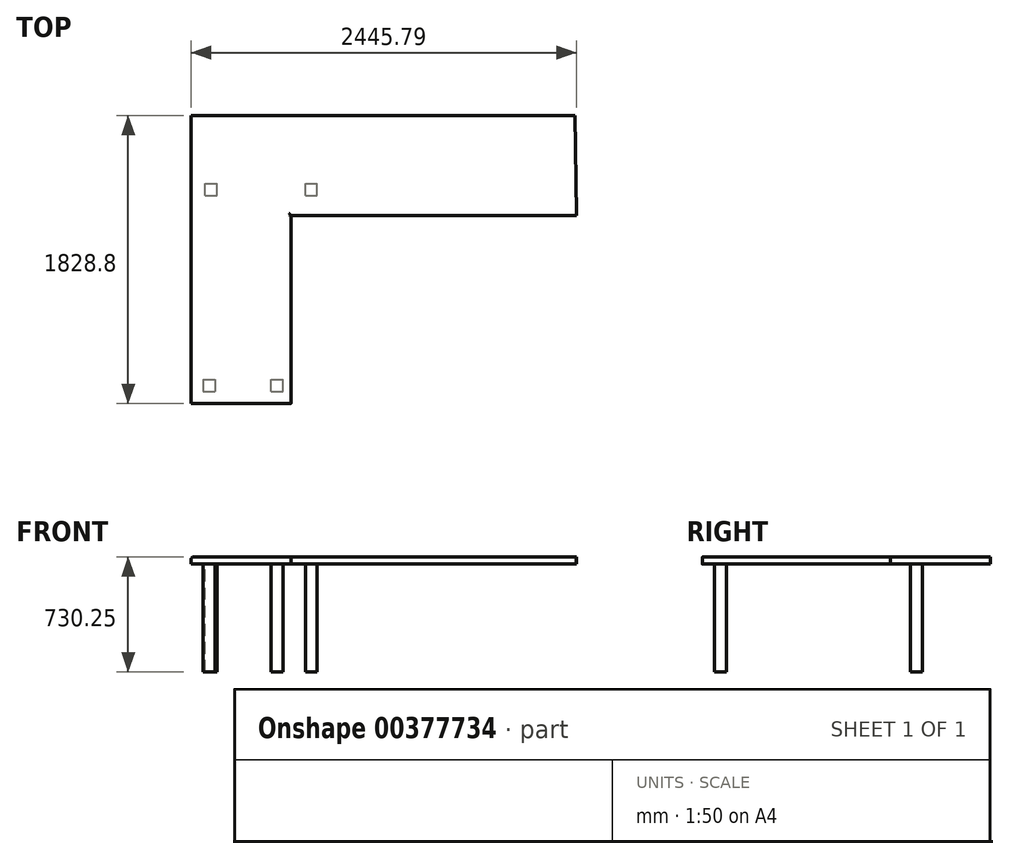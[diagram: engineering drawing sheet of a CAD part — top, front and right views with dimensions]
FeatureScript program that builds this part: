
annotation { "Feature Type Name" : "Feature", "Feature Type Description" : "" }
export const myFeature = defineFeature(function(context is Context, id is Id, definition is map)
    precondition{}
    {
        {
            var Q0;
            Q0=qCreatedBy(makeId("Top.planeOp"),FACE);
            var sketch = newSketch(context, id + "F0", { "sketchPlane" : qUnion([Q0])});
            skLineSegment(sketch, "E0", {"start": v(2399.33, 1785.57) * mm, "end": v(-39.07, 1785.57) * mm});
            skLineSegment(sketch, "E1", {"start": v(-39.07, 1785.57) * mm, "end": v(-39.07, -43.23) * mm});
            skLineSegment(sketch, "E2", {"start": v(-39.07, -43.23) * mm, "end": v(595.93, -43.23) * mm});
            skLineSegment(sketch, "E3", {"start": v(595.93, -43.23) * mm, "end": v(595.93, 1150.61) * mm});
            skLineSegment(sketch, "E4", {"start": v(595.93, 1150.61) * mm, "end": v(2406.72, 1150.61) * mm});
            skLineSegment(sketch, "E5", {"start": v(2406.72, 1150.61) * mm, "end": v(2399.33, 1785.57) * mm});
            skSolve(sketch);
        }
        {
            var Q0;
            Q0 = qSketchRegion(id + "F0", true);
            extrude(context, id + "F1", {"entities" : qUnion([Q0]), "depth" : 44.45 * mm});
        }
        {
            var Q0;
            Q0=makeQuery(id+"F1.opExtrude","CAP_EDGE",EDGE,{"disambiguationData":[OSD([sQuery(id+"F0.wireOp",EDGE,"E3")])],"isStart":false});
            var Q1;
            Q1=makeQuery(id+"F1.opExtrude","CAP_EDGE",EDGE,{"disambiguationData":[OSD([sQuery(id+"F0.wireOp",EDGE,"i6ojEBDx-LtBP-nYZZ-NaNR-S9qS1XHOSYIY")])],"isStart":true});
            var Q2;
            Q2=makeQuery(id+"F1.opExtrude","CAP_EDGE",EDGE,{"disambiguationData":[OSD([sQuery(id+"F0.wireOp",EDGE,"E4")])],"isStart":false});
            var Q3;
            Q3=makeQuery(id+"F1.opExtrude","CAP_EDGE",EDGE,{"disambiguationData":[OSD([sQuery(id+"F0.wireOp",EDGE,"E1")])],"isStart":false});
            fillet(context, id + "F2", {"entities" : qUnion([Q0, Q1, Q2, Q3]), "radius" : 12.7 * mm, "tangentPropagation" : true, "allowEdgeOverflow" : false});
        }
        {
            var Q0;
            Q0=makeQuery(id+"F1.opExtrude","CAP_EDGE",EDGE,{"disambiguationData":[OSD([sQuery(id+"F0.wireOp",EDGE,"E3")])],"isStart":true});
            fillet(context, id + "F3", {"entities" : qUnion([Q0]), "radius" : 17.78 * mm, "tangentPropagation" : true, "allowEdgeOverflow" : false});
        }
        {
            var Q0;
            Q0=makeQuery(id+"F1.opExtrude","CAP_FACE",FACE,{"disambiguationData":[OSD([sQuery(id+"F0.wireOp",EDGE,"E0"),sQuery(id+"F0.wireOp",EDGE,"E1"),sQuery(id+"F0.wireOp",EDGE,"E2"),sQuery(id+"F0.wireOp",EDGE,"E3"),sQuery(id+"F0.wireOp",EDGE,"E4"),sQuery(id+"F0.wireOp",EDGE,"E5")])],"isStart":true});
            var sketch = newSketch(context, id + "F4", { "sketchPlane" : qUnion([Q0])});
            skLineSegment(sketch, "E6.bottom", {"start": v(37.13, -109.17) * mm, "end": v(113.33, -109.17) * mm});
            skLineSegment(sketch, "E6.top", {"start": v(37.13, -32.97) * mm, "end": v(113.33, -32.97) * mm});
            skLineSegment(sketch, "E6.left", {"start": v(37.13, -109.17) * mm, "end": v(37.13, -32.97) * mm});
            skLineSegment(sketch, "E6.right", {"start": v(113.33, -109.17) * mm, "end": v(113.33, -32.97) * mm});
            skLineSegment(sketch, "E7.bottom", {"start": v(468.93, -32.97) * mm, "end": v(545.13, -32.97) * mm});
            skLineSegment(sketch, "E7.top", {"start": v(468.93, -109.17) * mm, "end": v(545.13, -109.17) * mm});
            skLineSegment(sketch, "E7.left", {"start": v(468.93, -32.97) * mm, "end": v(468.93, -109.17) * mm});
            skLineSegment(sketch, "E7.right", {"start": v(545.13, -32.97) * mm, "end": v(545.13, -109.17) * mm});
            skLineSegment(sketch, "E8.bottom", {"start": v(50.08, -1278.67) * mm, "end": v(125.18, -1278.67) * mm});
            skLineSegment(sketch, "E8.top", {"start": v(50.08, -1353.77) * mm, "end": v(125.18, -1353.77) * mm});
            skLineSegment(sketch, "E8.left", {"start": v(50.08, -1278.67) * mm, "end": v(50.08, -1353.77) * mm});
            skLineSegment(sketch, "E8.right", {"start": v(125.18, -1278.67) * mm, "end": v(125.18, -1353.77) * mm});
            skLineSegment(sketch, "E9.bottom", {"start": v(686.18, -1278.67) * mm, "end": v(761.28, -1278.67) * mm});
            skLineSegment(sketch, "E9.top", {"start": v(686.18, -1353.77) * mm, "end": v(761.28, -1353.77) * mm});
            skLineSegment(sketch, "E9.left", {"start": v(686.18, -1278.67) * mm, "end": v(686.18, -1353.77) * mm});
            skLineSegment(sketch, "E9.right", {"start": v(761.28, -1278.67) * mm, "end": v(761.28, -1353.77) * mm});
            skSolve(sketch);
        }
        {
            var Q0;
            Q0=makeQuery(id+"F4.imprint","IMPRINT",FACE,{"disambiguationData":[TD([[makeQuery(id+"F4.imprint","IMPRINT",EDGE,{"derivedFrom":sQuery(id+"F4.wireOp",EDGE,"E6.bottom")}),1.0]])]});
            var Q1;
            Q1=makeQuery(id+"F4.imprint","IMPRINT",FACE,{"disambiguationData":[TD([[makeQuery(id+"F4.imprint","IMPRINT",EDGE,{"derivedFrom":sQuery(id+"F4.wireOp",EDGE,"E7.bottom")}),-1.0]])]});
            var Q2;
            Q2=makeQuery(id+"F4.imprint","IMPRINT",FACE,{"disambiguationData":[TD([[makeQuery(id+"F4.imprint","IMPRINT",EDGE,{"derivedFrom":sQuery(id+"F4.wireOp",EDGE,"E9.bottom")}),-1.0]])]});
            var Q3;
            Q3=makeQuery(id+"F4.imprint","IMPRINT",FACE,{"disambiguationData":[TD([[makeQuery(id+"F4.imprint","IMPRINT",EDGE,{"derivedFrom":sQuery(id+"F4.wireOp",EDGE,"E8.bottom")}),-1.0]])]});
            extrude(context, id + "F5", {"entities" : qUnion([Q0, Q1, Q2, Q3]), "operationType" : NewBodyOperationType.ADD, "depth" : 685.8 * mm, "offsetDistance" : 25.4 * mm});
        }
    });
